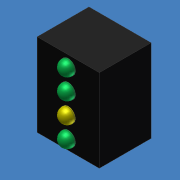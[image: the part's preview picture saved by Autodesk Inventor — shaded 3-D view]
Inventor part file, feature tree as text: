
AUTODESK INVENTOR PART (.ipt)
format: ipt  version: 2011 (Build 150239000, 239)  size: 125,440 bytes
history: native  units: mm (DEFAULTED — no unit token found)
features: extrude x5, fillet x4, sketch x2
ambient origin geometry x8: Origin, YZ Plane, XZ Plane, XY Plane, X Axis, Y Axis, Z Axis, Center Point
bodies: Solid1 (feature_tree)
feature tree (11):
  extrude  "Extrusion1"  Depth=10.16mm
  sketch  "Sketch2"  dims[d2=6.35mm d3=0.0mm d4=1.27mm d5=1.778mm d6=1.016mm d7=0.0mm d8=0.889mm d12=40.0mm d14=2.54mm d15=10.0mm d17=25.4mm d19=1.016mm d20=0.0mm d21=0.889mm d22=1.016mm d23=0.0mm d24=0.889mm d25=1.016mm d26=0.0mm d27=0.889mm]
  extrude  "Extrusion2"  Depth=1.27mm
  fillet  "Fillet1"  Radius=1.778mm
  extrude  "Extrusion3"  Depth=1.016mm TaperAngle=0.0deg
  fillet  "Fillet2"  Radius=0.889mm
  extrude  "Extrusion4"  Depth=40.0mm
  fillet  "Fillet3"  Radius=1.016mm
  extrude  "Extrusion5"  Depth=0.889mm
  fillet  "Fillet4"  Radius=1.016mm
  sketch  "Sketch1"  dims[d0=7.62mm d1=10.16mm]
